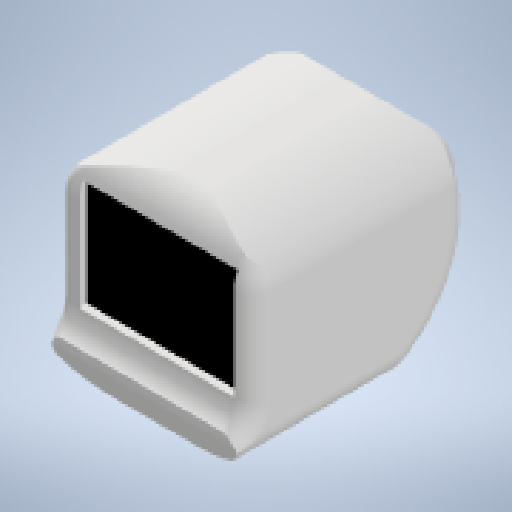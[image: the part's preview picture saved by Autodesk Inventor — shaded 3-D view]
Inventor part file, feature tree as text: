
AUTODESK INVENTOR PART (.ipt)
format: ipt  version: 2024 (Build 280153000, 153)  size: 422,912 bytes
history: native  units: in
note: dims shown in document units (in); Inventor stores cm internally (conversion verified against a paired STEP export)
features: fillet x11, extrude x6, sketch x6, chamfer x1
ambient origin geometry x8: Origin, YZ Plane, XZ Plane, XY Plane, X Axis, Y Axis, Z Axis, Center Point
bodies: Solid1 (feature_tree)
feature tree (24):
  extrude  "Extrusion1"  Depth=25.0in
  extrude  "Extrusion2"  Depth=30.0in TaperAngle=0.0deg
  extrude  "Extrusion3"  Depth=20.0in
  extrude  "Extrusion4"  Depth=2.5in
  fillet  "Fillet2"  Radius=1.0in
  fillet  "Fillet3"  Radius=3.0in
  fillet  "Fillet5"  Radius=2.0in
  fillet  "Fillet6"  Radius=1.5in
  extrude  "Extrusion5"  Depth=12.5in
  chamfer  "Chamfer1"  Distance=10.0in
  extrude  "Extrusion6"  Depth=2.0in TaperAngle=45.0deg
  fillet  "Fillet7"  Radius=12.5in
  fillet  "Fillet8"  Radius=10.0in
  fillet  "Fillet9"  Radius=2.0in
  fillet  "Fillet10"  Radius=2.0in
  fillet  "Fillet13"  Radius=3.0in
  fillet  "Fillet14"  Radius=3.0in
  fillet  "Fillet15"  Radius=2.5in
  sketch  "Sketch1"  dims[d0=25.0in d1=25.0in]
  sketch  "Sketch2"  dims[d2=30.0in d3=0.0in d6=30.0in d7=0.0in]
  sketch  "Sketch3"  dims[d8=30.0in d9=0.0in d10=20.0in]
  sketch  "Sketch4"  dims[d11=14.0in d12=2.5in d13=1.0in d14=0.0in d16=3.0in d17=2.0in d19=1.5in]
  sketch  "Sketch5"  dims[d20=5.0in d21=12.5in d22=10.0in d23=0.0in]
  sketch  "Sketch7"  dims[d24=25.0in d25=0.0in d26=2.0in d27=0.125in d28=45.0deg d29=12.5in d30=10.0in d31=30.0in d32=0.0in d33=0.0in d34=2.0in d35=2.0in d36=3.0in d37=3.0in d40=2.5in d41=1.3in d44=0.5in d39=0.0in d42=0.0in d45=0.0in d46=0.0in d47=0.0in d48=0.0in]
